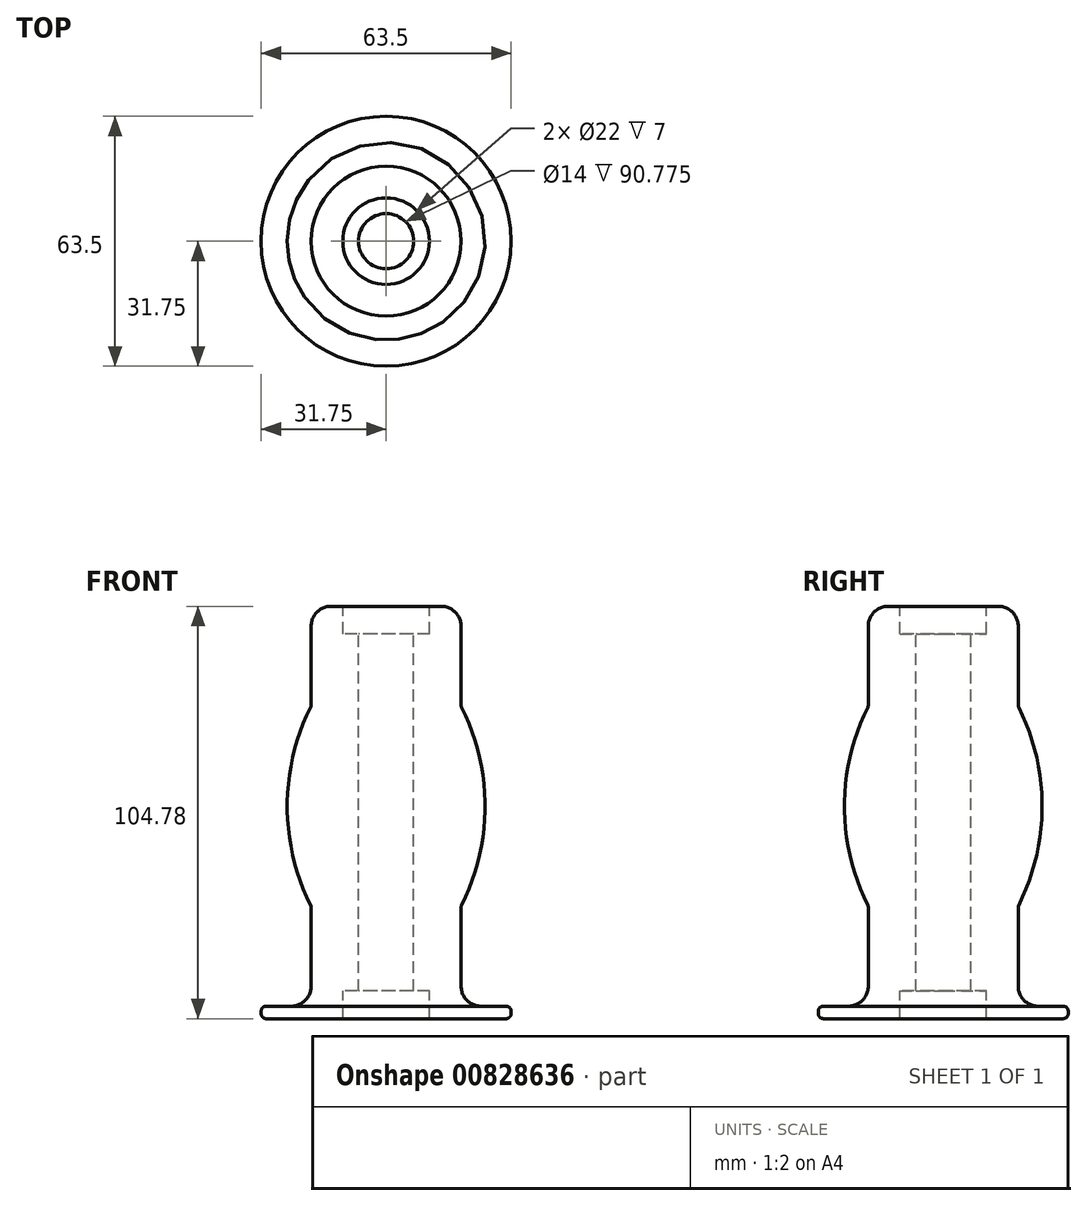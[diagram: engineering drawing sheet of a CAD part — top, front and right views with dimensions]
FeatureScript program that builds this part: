
annotation { "Feature Type Name" : "Feature", "Feature Type Description" : "" }
export const myFeature = defineFeature(function(context is Context, id is Id, definition is map)
    precondition{}
    {
        {
            var Q0;
            Q0=qCreatedBy(makeId("Front.planeOp"),FACE);
            var sketch = newSketch(context, id + "F0", { "sketchPlane" : qUnion([Q0])});
            skLineSegment(sketch, "E0", {"start": v(-7, 7) * mm, "end": v(-11, 7) * mm});
            skLineSegment(sketch, "E1", {"start": v(-11, 7) * mm, "end": v(-11, 0) * mm});
            skLineSegment(sketch, "E2", {"start": v(-11, 0) * mm, "end": v(-31.75, 0) * mm});
            skLineSegment(sketch, "E3", {"start": v(-31.75, 0) * mm, "end": v(-31.75, 3.17) * mm});
            skLineSegment(sketch, "E4", {"start": v(-31.75, 3.17) * mm, "end": v(-19.05, 3.17) * mm});
            skLineSegment(sketch, "E5", {"start": v(-19.05, 3.17) * mm, "end": v(-19.05, 28.58) * mm});
            skLineSegment(sketch, "E6", {"start": v(-19.05, 104.78) * mm, "end": v(-11, 104.78) * mm});
            skLineSegment(sketch, "E7", {"start": v(-11, 104.78) * mm, "end": v(-11, 97.78) * mm});
            skLineSegment(sketch, "E8", {"start": v(-11, 97.78) * mm, "end": v(-7, 97.78) * mm});
            skLineSegment(sketch, "E9", {"start": v(0, 97.77) * mm, "end": v(0, 7) * mm, "construction": true});
            skArc(sketch, "E10", {"start": v(-19.05, 79.37) * mm, "mid": v(-25.13, 53.97) * mm, "end": v(-19.05, 28.57) * mm});
            skLineSegment(sketch, "E11.trimOffspring", {"start": v(-19.05, 79.38) * mm, "end": v(-19.05, 104.78) * mm});
            skLineSegment(sketch, "E12", {"start": v(-19.05, 104.78) * mm, "end": v(-19.05, 3.17) * mm, "construction": true});
            skPoint(sketch, "E13", {"position": v(-19.05, 53.98) * mm});
            skLineSegment(sketch, "E14", {"start": v(-67.83, 53.98) * mm, "end": v(32.24, 53.98) * mm, "construction": true});
            skLineSegment(sketch, "E15", {"start": v(-25.4, 71.4) * mm, "end": v(-25.4, 23.54) * mm, "construction": true});
            skLineSegment(sketch, "E16", {"start": v(-7, 97.78) * mm, "end": v(-7, 7) * mm});
            skSolve(sketch);
        }
        {
            var Q0;
            Q0=makeQuery(id+"F0.imprint","IMPRINT",FACE,{"disambiguationData":[TD([[makeQuery(id+"F0.imprint","IMPRINT",EDGE,{"derivedFrom":sQuery(id+"F0.wireOp",EDGE,"E0")}),-1.0]])]});
            var Q1;
            Q1=sQuery(id+"F0.wireOp",EDGE,"E9");
            revolve(context, id + "F1", {"surfaceOperationType" : NewSurfaceOperationType.NEW, "entities" : qUnion([Q0]), "axis" : qUnion([Q1]), "revolveType" : RevolveType.FULL});
        }
        {
            var Q0;
            Q0=makeQuery(id+"F1.opRevolve","SWEPT_EDGE",EDGE,{"disambiguationData":[OSD([sQuery(id+"F0.wireOp",EDGE,"E6"),sQuery(id+"F0.wireOp",EDGE,"E11.trimOffspring")])]});
            var Q1;
            Q1=makeQuery(id+"F1.opRevolve","SWEPT_EDGE",EDGE,{"disambiguationData":[OSD([sQuery(id+"F0.wireOp",EDGE,"E4"),sQuery(id+"F0.wireOp",EDGE,"E5")])]});
            fillet(context, id + "F2", {"entities" : qUnion([Q0, Q1]), "radius" : 5.08 * mm, "tangentPropagation" : true, "allowEdgeOverflow" : false});
        }
        {
            var Q0;
            Q0=makeQuery(id+"F1.opRevolve","SWEPT_EDGE",EDGE,{"disambiguationData":[OSD([sQuery(id+"F0.wireOp",EDGE,"E3"),sQuery(id+"F0.wireOp",EDGE,"E4")])]});
            var Q1;
            Q1=makeQuery(id+"F1.opRevolve","SWEPT_EDGE",EDGE,{"disambiguationData":[OSD([sQuery(id+"F0.wireOp",EDGE,"E2"),sQuery(id+"F0.wireOp",EDGE,"E3")])]});
            var Q2;
            Q2=makeQuery(id+"F1.opRevolve","SWEPT_EDGE",EDGE,{"disambiguationData":[OSD([sQuery(id+"F0.wireOp",EDGE,"E5"),sQuery(id+"F0.wireOp",EDGE,"E10")])]});
            var Q3;
            Q3=makeQuery(id+"F1.opRevolve","SWEPT_EDGE",EDGE,{"disambiguationData":[OSD([sQuery(id+"F0.wireOp",EDGE,"E10"),sQuery(id+"F0.wireOp",EDGE,"E11.trimOffspring")])]});
            fillet(context, id + "F3", {"entities" : qUnion([Q0, Q1, Q2, Q3]), "radius" : 1.27 * mm, "tangentPropagation" : true, "allowEdgeOverflow" : false});
        }
    });
